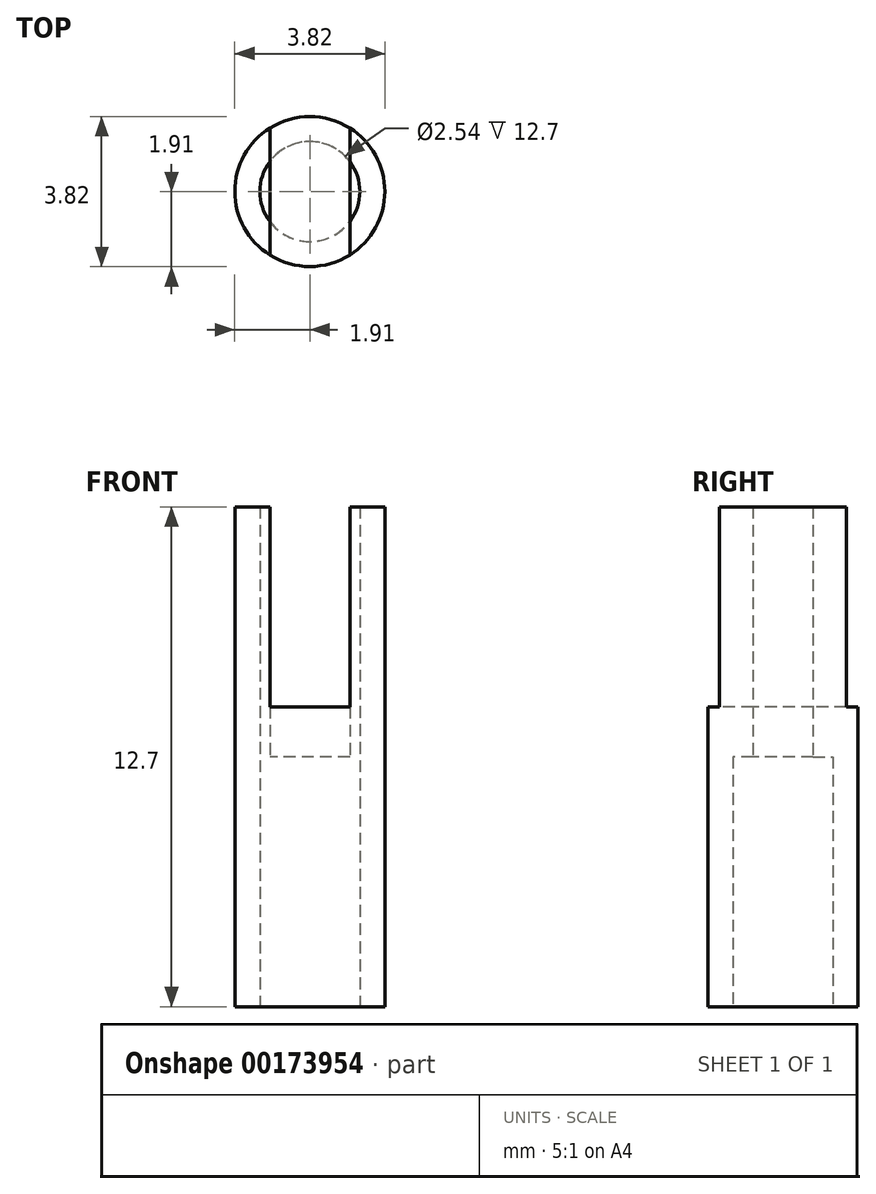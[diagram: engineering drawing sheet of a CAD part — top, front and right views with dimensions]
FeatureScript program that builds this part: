
annotation { "Feature Type Name" : "Feature", "Feature Type Description" : "" }
export const myFeature = defineFeature(function(context is Context, id is Id, definition is map)
    precondition{}
    {
        {
            var Q0;
            Q0=qCreatedBy(makeId("Top.planeOp"),FACE);
            var sketch = newSketch(context, id + "F0", { "sketchPlane" : qUnion([Q0])});
            skCircle(sketch, "E0", {"center": v(0, 0) * mm, "radius": 1.27 * mm});
            skCircle(sketch, "E1", {"center": v(0, 0) * mm, "radius": 1.9 * mm});
            skSolve(sketch);
        }
        {
            var Q0;
            Q0 = qSketchRegion(id + "F0", true);
            extrude(context, id + "F1", {"entities" : qUnion([Q0]), "depth" : 12.7 * mm});
        }
        {
            var Q0;
            Q0=qCreatedBy(makeId("Front.planeOp"),FACE);
            var sketch = newSketch(context, id + "F2", { "sketchPlane" : qUnion([Q0])});
            skLineSegment(sketch, "E2.bottom", {"start": v(1.02, 20.06) * mm, "end": v(-1.02, 20.06) * mm});
            skLineSegment(sketch, "E2.top", {"start": v(1.02, 6.35) * mm, "end": v(-1.02, 6.35) * mm});
            skLineSegment(sketch, "E2.left", {"start": v(1.02, 20.06) * mm, "end": v(1.02, 6.35) * mm});
            skLineSegment(sketch, "E2.right", {"start": v(-1.02, 20.06) * mm, "end": v(-1.02, 6.35) * mm});
            skPoint(sketch, "E2.middle", {"position": v(0, 13.2) * mm});
            skSolve(sketch);
        }
        {
            var Q0;
            Q0 = qSketchRegion(id + "F2", true);
            extrude(context, id + "F3", {"entities" : qUnion([Q0]), "operationType" : NewBodyOperationType.REMOVE, "endBound" : BoundingType.SYMMETRIC, "oppositeDirection" : true, "depth" : 25.4 * mm});
        }
        {
            var Q0;
            Q0=makeQuery(id+"F3.boolean.opBoolean","COPY",FACE,{"disambiguationData":[OD(0.0)],"derivedFrom":makeQuery(id+"F3.opExtrude","SWEPT_FACE",FACE,{"disambiguationData":[OSD([sQuery(id+"F2.wireOp",EDGE,"E2.top")])]})});
            var sketch = newSketch(context, id + "F4", { "sketchPlane" : qUnion([Q0])});
            skArc(sketch, "E3.0", {"start": v(-1.02, -1.61) * mm, "mid": v(0, -1.9) * mm, "end": v(1.02, -1.61) * mm});
            skArc(sketch, "E3.1", {"start": v(1.02, 1.61) * mm, "mid": v(0, 1.9) * mm, "end": v(-1.02, 1.61) * mm});
            skLineSegment(sketch, "E4", {"start": v(-1.02, 1.61) * mm, "end": v(-1.02, -1.61) * mm});
            skLineSegment(sketch, "E5", {"start": v(1.02, -1.61) * mm, "end": v(1.02, 1.61) * mm});
            skSolve(sketch);
        }
        {
            var Q0;
            Q0 = qSketchRegion(id + "F4", true);
            extrude(context, id + "F5", {"entities" : qUnion([Q0]), "operationType" : NewBodyOperationType.ADD, "depth" : 1.27 * mm});
        }
    });
